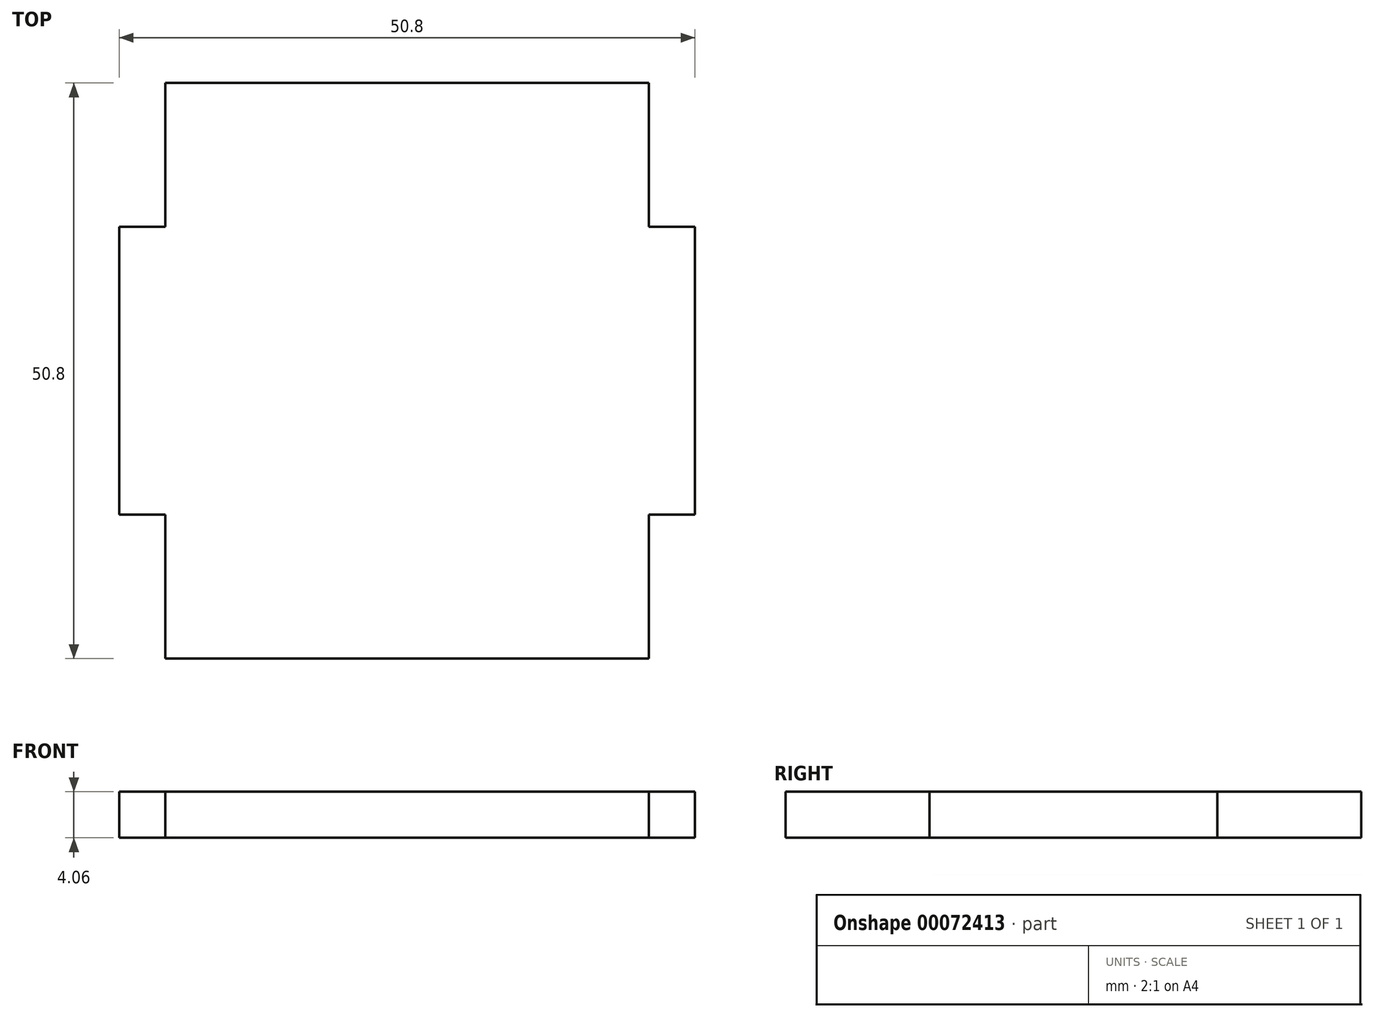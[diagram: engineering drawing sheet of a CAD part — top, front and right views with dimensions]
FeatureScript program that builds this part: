
annotation { "Feature Type Name" : "Feature", "Feature Type Description" : "" }
export const myFeature = defineFeature(function(context is Context, id is Id, definition is map)
    precondition{}
    {
        {
            var Q0;
            Q0=qCreatedBy(makeId("Top.planeOp"),FACE);
            var sketch = newSketch(context, id + "F0", { "sketchPlane" : qUnion([Q0])});
            skLineSegment(sketch, "E0.rect.bottom", {"start": v(21.34, 25.4) * mm, "end": v(-21.34, 25.4) * mm});
            skLineSegment(sketch, "E0.rect.top", {"start": v(21.34, -25.4) * mm, "end": v(-21.34, -25.4) * mm});
            skLineSegment(sketch, "E0.rect.left", {"start": v(21.34, 25.4) * mm, "end": v(21.34, -25.4) * mm});
            skLineSegment(sketch, "E0.rect.right", {"start": v(-21.34, 25.4) * mm, "end": v(-21.34, -25.4) * mm});
            skPoint(sketch, "E0.rect.middle", {"position": v(0, 0) * mm});
            skLineSegment(sketch, "E1.rect.bottom", {"start": v(-17.27, 12.7) * mm, "end": v(-25.4, 12.7) * mm});
            skLineSegment(sketch, "E1.rect.top", {"start": v(-17.27, -12.7) * mm, "end": v(-25.4, -12.7) * mm});
            skLineSegment(sketch, "E1.rect.left", {"start": v(-17.27, 12.7) * mm, "end": v(-17.27, -12.7) * mm});
            skLineSegment(sketch, "E1.rect.right", {"start": v(-25.4, 12.7) * mm, "end": v(-25.4, -12.7) * mm});
            skPoint(sketch, "E1.rect.middle", {"position": v(-21.34, 0) * mm});
            skLineSegment(sketch, "E2", {"start": v(0, 34.9) * mm, "end": v(0, -33.79) * mm, "construction": true});
            skLineSegment(sketch, "E3", {"start": v(-36.9, 0) * mm, "end": v(40.56, 0) * mm, "construction": true});
            skLineSegment(sketch, "E4.MirrorCS", {"start": v(25.4, 12.7) * mm, "end": v(25.4, -12.7) * mm});
            skLineSegment(sketch, "E5.MirrorCS", {"start": v(17.27, 12.7) * mm, "end": v(25.4, 12.7) * mm});
            skLineSegment(sketch, "E6.MirrorCS", {"start": v(17.27, 12.7) * mm, "end": v(17.27, -12.7) * mm});
            skLineSegment(sketch, "E7.MirrorCS", {"start": v(17.27, -12.7) * mm, "end": v(25.4, -12.7) * mm});
            skSolve(sketch);
        }
        {
            var Q0;
            {var subQ11=sQuery(id+"F0.wireOp",EDGE,"E0.rect.bottom");Q0=makeQuery(id+"F0.imprint","IMPRINT",FACE,{"disambiguationData":[TD([[makeQuery(id+"F0.imprint","IMPRINT",EDGE,{"derivedFrom":subQ11}),1.0]])]});}
            var Q1;
            {var subQ5=sQuery(id+"F0.wireOp",EDGE,"E6.MirrorCS");Q1=makeQuery(id+"F0.imprint","IMPRINT",FACE,{"disambiguationData":[TD([[makeQuery(id+"F0.imprint","IMPRINT",EDGE,{"derivedFrom":subQ5}),1.0]])]});}
            var Q2;
            {var subQ5=sQuery(id+"F0.wireOp",EDGE,"E4.MirrorCS");Q2=makeQuery(id+"F0.imprint","IMPRINT",FACE,{"disambiguationData":[TD([[makeQuery(id+"F0.imprint","IMPRINT",EDGE,{"derivedFrom":subQ5}),-1.0]])]});}
            var Q3;
            {var subQ5=sQuery(id+"F0.wireOp",EDGE,"E1.rect.right");Q3=makeQuery(id+"F0.imprint","IMPRINT",FACE,{"disambiguationData":[TD([[makeQuery(id+"F0.imprint","IMPRINT",EDGE,{"derivedFrom":subQ5}),1.0]])]});}
            var Q4;
            {var subQ5=sQuery(id+"F0.wireOp",EDGE,"E1.rect.left");Q4=makeQuery(id+"F0.imprint","IMPRINT",FACE,{"disambiguationData":[TD([[makeQuery(id+"F0.imprint","IMPRINT",EDGE,{"derivedFrom":subQ5}),-1.0]])]});}
            extrude(context, id + "F1", {"entities" : qUnion([Q0, Q1, Q2, Q3, Q4]), "depth" : 4.06 * mm});
        }
    });
